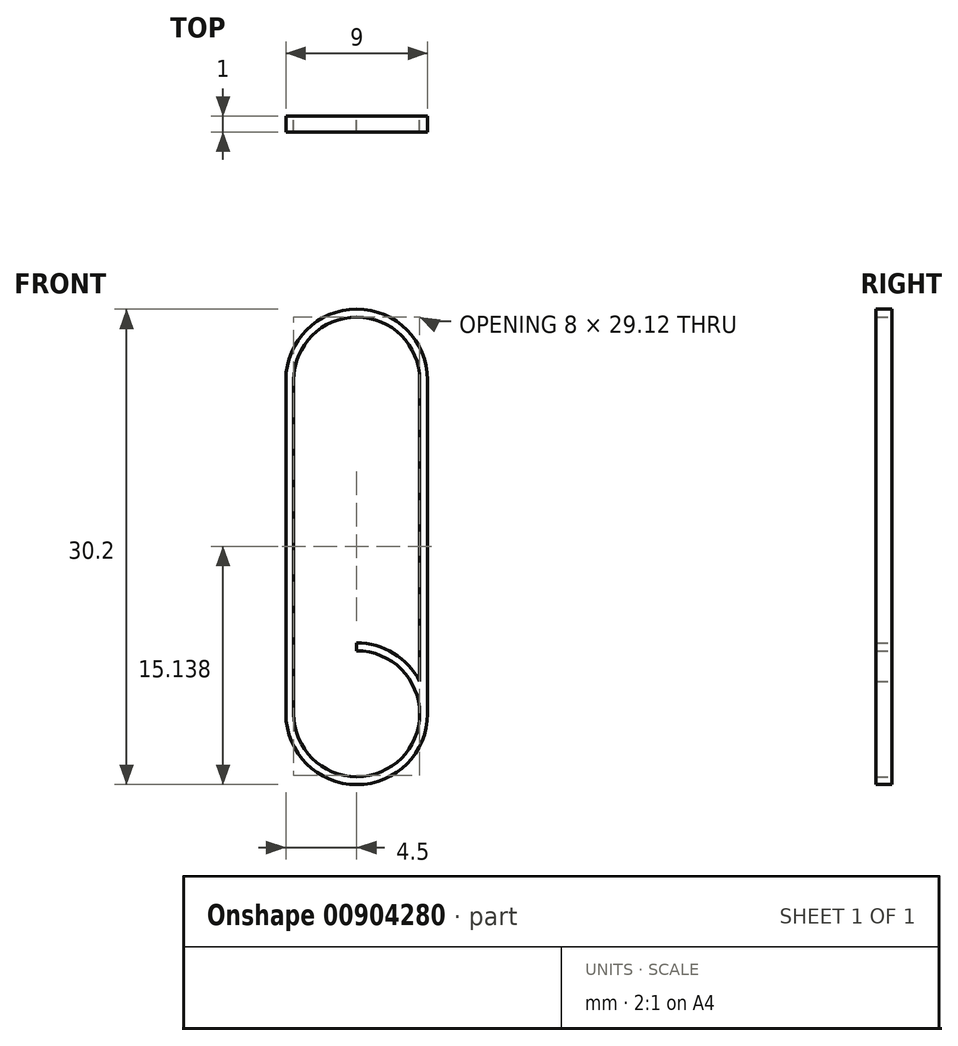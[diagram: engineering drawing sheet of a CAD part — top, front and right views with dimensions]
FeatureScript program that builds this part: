
annotation { "Feature Type Name" : "Feature", "Feature Type Description" : "" }
export const myFeature = defineFeature(function(context is Context, id is Id, definition is map)
    precondition{}
    {
        {
            var Q0;
            Q0=qCreatedBy(makeId("Front.planeOp"),FACE);
            var sketch = newSketch(context, id + "F0", { "sketchPlane" : qUnion([Q0])});
            skCircle(sketch, "E0", {"center": v(0, 0) * mm, "radius": 4 * mm});
            skLineSegment(sketch, "E1", {"start": v(0, 0) * mm, "end": v(0, 21.2) * mm});
            skCircle(sketch, "E2", {"center": v(0, 21.2) * mm, "radius": 4 * mm});
            skLineSegment(sketch, "E3", {"start": v(0, 21.2) * mm, "end": v(4, 21.2) * mm});
            skLineSegment(sketch, "E4", {"start": v(4, 21.2) * mm, "end": v(-4, 21.2) * mm});
            skLineSegment(sketch, "E5", {"start": v(-4, 21.2) * mm, "end": v(0, 21.2) * mm});
            skLineSegment(sketch, "E6", {"start": v(0, 0) * mm, "end": v(4, 0) * mm});
            skLineSegment(sketch, "E7", {"start": v(4, 0) * mm, "end": v(-4, 0) * mm});
            skLineSegment(sketch, "E8", {"start": v(-4, 0) * mm, "end": v(0, 0) * mm});
            skLineSegment(sketch, "E9", {"start": v(-4, 21.2) * mm, "end": v(-4, 0) * mm});
            skLineSegment(sketch, "E10", {"start": v(4, 21.2) * mm, "end": v(4, 0) * mm});
            skCircle(sketch, "E11", {"center": v(0, 21.2) * mm, "radius": 4.5 * mm});
            skCircle(sketch, "E12", {"center": v(0, 0) * mm, "radius": 4.5 * mm});
            skLineSegment(sketch, "E13", {"start": v(0, 0) * mm, "end": v(-4.5, 0) * mm});
            skPoint(sketch, "E13.endSnap0", {"position": v(-2, 0) * mm});
            skLineSegment(sketch, "E14", {"start": v(-4.5, 0) * mm, "end": v(4.5, 0) * mm});
            skLineSegment(sketch, "E15", {"start": v(4.5, 0) * mm, "end": v(0, 0) * mm});
            skLineSegment(sketch, "E16", {"start": v(0, 21.2) * mm, "end": v(4.5, 21.2) * mm});
            skLineSegment(sketch, "E17", {"start": v(4.5, 21.2) * mm, "end": v(-4.5, 21.2) * mm});
            skLineSegment(sketch, "E18", {"start": v(-4.5, 21.2) * mm, "end": v(0, 21.2) * mm});
            skLineSegment(sketch, "E19", {"start": v(-4.5, 21.2) * mm, "end": v(-4.5, 0) * mm});
            skLineSegment(sketch, "E20", {"start": v(4.5, 0) * mm, "end": v(4.5, 21.2) * mm});
            skSolve(sketch);
        }
        {
            var Q0;
            {var subQ0=sQuery(id+"F0.wireOp",EDGE,"E18");var subQ1=sQuery(id+"F0.wireOp",EDGE,"E2");var subQ2=makeQuery(id+"F0.imprint","INTERSECT",VERTEX,{"derivedFrom":[subQ1,sQuery(id+"F0.wireOp",EDGE,"E9"),subQ0]});Q0=makeQuery(id+"F0.imprint","IMPRINT",FACE,{"disambiguationData":[TD([[makeQuery(id+"F0.imprint","IMPRINT",EDGE,{"disambiguationData":[TD([[subQ2,1.0]])],"derivedFrom":subQ1}),-1.0]])]});}
            var Q1;
            {var subQ1=sQuery(id+"F0.wireOp",EDGE,"E10");var subQ3=sQuery(id+"F0.wireOp",EDGE,"E11");var subQ4=makeQuery(id+"F0.imprint","INTERSECT",VERTEX,{"derivedFrom":[subQ1,subQ3]});Q1=makeQuery(id+"F0.imprint","IMPRINT",FACE,{"disambiguationData":[TD([[makeQuery(id+"F0.imprint","IMPRINT",EDGE,{"disambiguationData":[TD([[subQ4,1.0]])],"derivedFrom":subQ1}),1.0]])]});}
            var Q2;
            {var subQ1=sQuery(id+"F0.wireOp",EDGE,"E9");var subQ3=sQuery(id+"F0.wireOp",EDGE,"E11");var subQ4=makeQuery(id+"F0.imprint","INTERSECT",VERTEX,{"derivedFrom":[subQ1,subQ3]});Q2=makeQuery(id+"F0.imprint","IMPRINT",FACE,{"disambiguationData":[TD([[makeQuery(id+"F0.imprint","IMPRINT",EDGE,{"disambiguationData":[TD([[subQ4,1.0]])],"derivedFrom":subQ1}),-1.0]])]});}
            var Q3;
            {var subQ5=sQuery(id+"F0.wireOp",EDGE,"E19");Q3=makeQuery(id+"F0.imprint","IMPRINT",FACE,{"disambiguationData":[TD([[makeQuery(id+"F0.imprint","IMPRINT",EDGE,{"derivedFrom":subQ5}),1.0]])]});}
            var Q4;
            {var subQ5=sQuery(id+"F0.wireOp",EDGE,"E20");Q4=makeQuery(id+"F0.imprint","IMPRINT",FACE,{"disambiguationData":[TD([[makeQuery(id+"F0.imprint","IMPRINT",EDGE,{"derivedFrom":subQ5}),1.0]])]});}
            var Q5;
            {var subQ1=sQuery(id+"F0.wireOp",EDGE,"E9");var subQ3=sQuery(id+"F0.wireOp",EDGE,"E12");var subQ4=makeQuery(id+"F0.imprint","INTERSECT",VERTEX,{"derivedFrom":[subQ1,subQ3]});Q5=makeQuery(id+"F0.imprint","IMPRINT",FACE,{"disambiguationData":[TD([[makeQuery(id+"F0.imprint","IMPRINT",EDGE,{"disambiguationData":[TD([[subQ4,-1.0]])],"derivedFrom":subQ1}),-1.0]])]});}
            var Q6;
            {var subQ1=sQuery(id+"F0.wireOp",EDGE,"E10");var subQ3=sQuery(id+"F0.wireOp",EDGE,"E12");var subQ4=makeQuery(id+"F0.imprint","INTERSECT",VERTEX,{"derivedFrom":[subQ1,subQ3]});Q6=makeQuery(id+"F0.imprint","IMPRINT",FACE,{"disambiguationData":[TD([[makeQuery(id+"F0.imprint","IMPRINT",EDGE,{"disambiguationData":[TD([[subQ4,-1.0]])],"derivedFrom":subQ1}),1.0]])]});}
            var Q7;
            {var subQ0=sQuery(id+"F0.wireOp",EDGE,"E14");var subQ1=sQuery(id+"F0.wireOp",EDGE,"E0");var subQ2=makeQuery(id+"F0.imprint","INTERSECT",VERTEX,{"derivedFrom":[subQ1,sQuery(id+"F0.wireOp",EDGE,"E9"),subQ0]});Q7=makeQuery(id+"F0.imprint","IMPRINT",FACE,{"disambiguationData":[TD([[makeQuery(id+"F0.imprint","IMPRINT",EDGE,{"disambiguationData":[TD([[subQ2,-1.0]])],"derivedFrom":subQ1}),-1.0]])]});}
            extrude(context, id + "F1", {"entities" : qUnion([Q0, Q1, Q2, Q3, Q4, Q5, Q6, Q7]), "depth" : 1 * mm, "offsetDistance" : 25 * mm});
        }
    });
